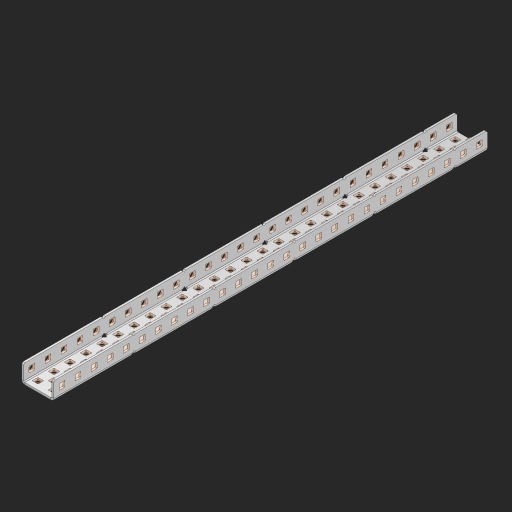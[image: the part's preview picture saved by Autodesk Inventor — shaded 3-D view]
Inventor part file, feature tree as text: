
AUTODESK INVENTOR PART (.ipt)
format: ipt  version: 2023 (Build 270158000, 158)  size: 1,725,440 bytes
history: native  units: in
note: dims shown in document units (in); Inventor stores cm internally (conversion verified against a paired STEP export)
features: other x142, extrude x133, sheet_metal_op x11, sketch x10, pattern_linear x2, mirror x1, chamfer x1
ambient origin geometry x8: Origin, YZ Plane, XZ Plane, XY Plane, X Axis, Y Axis, Z Axis, Center Point
bodies: Solid1 (feature_tree), Body (feature_tree)
feature tree (300):
  sheet_metal_op  "Flanges"
  other  "Flange Pattern Plane"
  other  "Flange Pattern Sketch"
  sheet_metal_op  "Flange Pattern"
  sheet_metal_op  "Body Pattern"
  pattern_linear  "Center Pattern"  Spacing1=0.0625in  [1 undecoded]
  other  "Arc Length"
  mirror  "Notch Mirror"
  pattern_linear  "Notch Pattern"  Spacing1=0.182in  [1 undecoded]
  chamfer  "End Chamfer"
  extrude  "Half Cut"  Depth=0.02in
  sketch  "Sketch1"  dims[d0=1.0in]
  other  "Plate1"
  sketch  "Sketch2"  dims[d1=13.5in]
  other  "Plate2"
  sheet_metal_op  "Bend1"
  sheet_metal_op  "Corner1"
  sketch  "Sketch3"  dims[d2=0.0625in]
  sketch  "Sketch7"  dims[d3=0.0625in]
  other  "Srf1"
  other  "Srf2"
  sketch  "Sketch8"  dims[d4=0.0312in]
  sketch  "Sketch9"  dims[d5=0.125in]
  other  "Srf91"
  sheet_metal_op  "Body Pattern Sketch"
  other  "Srf92"
  sketch  "Sketch13"  dims[d6=0.0625in]
  sketch  "Sketch14"  dims[d7=0.5in d8=90.0deg d9=0.0312in]
  sketch  "Sketch15"  dims[d10=0.25in]
  sketch  "Sketch16"  dims[d11=0.0625in d12=0.0625in d16=0.182in d17=0.02in d18=0.0625in d19=0.0in d20=0.25in d21=0.25in d38=10.6299in d40=0.5in d41=0.7874in d43=1.0in d46=0.172in d47=1.0in d48=0.0in d49=0.182in d50=0.02in d51=0.25in d52=0.25in d53=0.0625in d54=0.0in d55=0.172in d56=1.0in d57=0.0in d58=0.25in d60=10.6299in d62=0.5in d63=0.7874in d65=0.5in d85=0.1473in d86=0.1782in d88=0.04in d89=0.0625in d90=0.0in d91=0.04in d92=0.0491in d95=2.5in d96=0.04in d97=0.25in d98=45.0deg d99=0.25in d100=0.5in d101=0.0in d102=2.497in d106=0.182in d107=0.02in d108=0.5in d109=0.5in d110=0.0625in d111=0.0in d112=0.172in d113=0.5in d114=0.0in d117=0.5in d118=0.5in d119=0.5in]
  other  "Srf786"
  other  "Srf823"
  other  "Srf824"
  other  "Srf825"
  other  "Srf826"
  other  "Srf827"
  other  "Srf828"
  other  "Srf829"
  other  "Srf856"
  other  "Srf857"
  other  "Srf858"
  other  "Srf859"
  other  "Srf860"
  other  "Srf861"
  other  "Srf862"
  other  "Srf889"
  other  "Srf890"
  other  "Srf891"
  other  "Srf892"
  other  "Srf893"
  other  "Srf894"
  other  "Srf895"
  other  "Srf896"
  other  "Srf922"
  other  "Srf923"
  other  "Srf924"
  other  "Srf925"
  other  "Srf926"
  other  "Srf959"
  other  "Srf960"
  other  "Srf961"
  other  "Srf962"
  other  "Srf963"
  other  "Srf996"
  other  "Srf997"
  other  "Srf998"
  other  "Srf999"
  other  "Srf1000"
  other  "Srf1143"
  other  "Srf1144"
  other  "Srf1145"
  other  "Srf1146"
  other  "Srf1147"
  other  "Srf1148"
  other  "Srf1149"
  other  "Srf1150"
  other  "Srf1151"
  other  "Srf1152"
  other  "Srf1153"
  other  "Srf1154"
  other  "Srf1155"
  other  "Srf1156"
  other  "Srf1157"
  other  "Srf1158"
  other  "Srf1159"
  other  "Srf1160"
  other  "Srf1161"
  other  "Srf1162"
  other  "Srf1163"
  other  "Srf1164"
  other  "Srf1165"
  other  "Srf1166"
  other  "Srf1167"
  other  "Srf1168"
  other  "Srf1169"
  other  "Srf1170"
  other  "Srf1171"
  other  "Srf1172"
  other  "Srf1173"
  other  "Srf1174"
  other  "Srf1175"
  other  "Srf1176"
  other  "Srf1177"
  other  "Srf1178"
  other  "Srf1179"
  other  "Srf1180"
  other  "Srf1181"
  other  "Srf1182"
  other  "Srf1199"
  other  "Srf1200"
  other  "Srf1201"
  other  "Srf1202"
  other  "Srf1203"
  other  "Srf1204"
  other  "Srf1205"
  other  "Srf1206"
  other  "Srf1207"
  other  "Srf1208"
  other  "Srf1209"
  other  "Srf1210"
  other  "Srf1211"
  other  "Srf1212"
  other  "Srf1213"
  other  "Srf1214"
  other  "Srf1215"
  other  "Srf1216"
  other  "Srf1217"
  other  "Srf1218"
  other  "Srf1219"
  other  "Srf1220"
  other  "Srf1221"
  other  "Srf1222"
  other  "Srf1223"
  other  "Srf1224"
  other  "Srf1225"
  other  "Srf1226"
  other  "Srf1227"
  other  "Srf1228"
  other  "Srf1229"
  other  "Srf1230"
  other  "Srf1231"
  other  "Srf1232"
  other  "Srf1233"
  other  "Srf1234"
  other  "Srf1235"
  other  "Srf1236"
  other  "Srf1237"
  other  "Srf1238"
  other  "Srf1255"
  other  "Srf1256"
  other  "Srf1257"
  other  "Srf1258"
  other  "Srf1259"
  other  "Srf1260"
  other  "Srf1261"
  other  "Srf1262"
  other  "Srf1263"
  other  "Srf1264"
  other  "Srf1265"
  other  "Srf1266"
  other  "Srf1267"
  sheet_metal_op  "Flange Stamp"
  sheet_metal_op  "Flange Circle"
  sheet_metal_op  "Body Stamp"
  sheet_metal_op  "Body Circle"
  other  "Center Stamp"
  other  "Center Circle"
  sheet_metal_op  "Notch"
  extrude  "ExtrusionSrf2"  Depth=0.0625in
  extrude  "ExtrusionSrf92"  TaperAngle=0.0deg  [1 undecoded]
  extrude  "ExtrusionSrf823"  Depth=0.5in
  extrude  "ExtrusionSrf824"  Depth=0.5in
  extrude  "ExtrusionSrf825"  Depth=0.5in
  extrude  "ExtrusionSrf826"  Depth=0.5in
  extrude  "ExtrusionSrf827"  Depth=1.0in TaperAngle=0.0deg
  extrude  "ExtrusionSrf828"  Depth=0.5in
  extrude  "ExtrusionSrf829"  Depth=0.02in
  extrude  "ExtrusionSrf856"  Depth=0.5in
  extrude  "ExtrusionSrf857"  Depth=0.5in
  extrude  "ExtrusionSrf858"  Depth=0.0625in
  extrude  "ExtrusionSrf859"  TaperAngle=0.0deg  [1 undecoded]
  extrude  "ExtrusionSrf860"  Depth=0.5in
  extrude  "ExtrusionSrf861"  Depth=1.0in TaperAngle=0.0deg
  extrude  "ExtrusionSrf862"  Depth=0.5in
  extrude  "ExtrusionSrf889"  Depth=0.5in
  extrude  "ExtrusionSrf890"  Depth=0.5in
  extrude  "ExtrusionSrf891"  Depth=0.5in
  extrude  "ExtrusionSrf892"  Depth=0.5in
  extrude  "ExtrusionSrf893"  Depth=0.5in
  extrude  "ExtrusionSrf894"  Depth=0.0625in
  extrude  "ExtrusionSrf895"  TaperAngle=0.0deg  [1 undecoded]
  extrude  "ExtrusionSrf896"  Depth=0.5in
  extrude  "ExtrusionSrf922"  Depth=0.5in
  extrude  "ExtrusionSrf923"  Depth=2.5in
  extrude  "ExtrusionSrf924"  Depth=0.5in TaperAngle=45.0deg
  extrude  "ExtrusionSrf925"  Depth=0.5in
  extrude  "ExtrusionSrf926"  Depth=0.5in TaperAngle=0.0deg
  extrude  "ExtrusionSrf959"  Depth=0.5in
  extrude  "ExtrusionSrf960"  Depth=0.5in
  extrude  "ExtrusionSrf961"  Depth=0.02in
  extrude  "ExtrusionSrf962"  Depth=0.5in
  extrude  "ExtrusionSrf963"  Depth=0.5in
  extrude  "ExtrusionSrf996"  Depth=0.0625in
  extrude  "ExtrusionSrf997"  TaperAngle=0.0deg  [1 undecoded]
  extrude  "ExtrusionSrf998"  Depth=0.5in
  extrude  "ExtrusionSrf999"  Depth=0.5in TaperAngle=0.0deg
  extrude  "ExtrusionSrf1000"  Depth=0.5in
  extrude  "ExtrusionSrf1143"  Depth=0.5in
  extrude  "ExtrusionSrf1144"  Depth=0.5in
  extrude  "ExtrusionSrf1145"  [1 undecoded]
  extrude  "ExtrusionSrf1146"  [1 undecoded]
  extrude  "ExtrusionSrf1147"  [1 undecoded]
  extrude  "ExtrusionSrf1148"  [1 undecoded]
  extrude  "ExtrusionSrf1149"  [1 undecoded]
  extrude  "ExtrusionSrf1150"  [1 undecoded]
  extrude  "ExtrusionSrf1151"  [1 undecoded]
  extrude  "ExtrusionSrf1152"  [1 undecoded]
  extrude  "ExtrusionSrf1153"  [1 undecoded]
  extrude  "ExtrusionSrf1154"  [1 undecoded]
  extrude  "ExtrusionSrf1155"  [1 undecoded]
  extrude  "ExtrusionSrf1156"  [1 undecoded]
  extrude  "ExtrusionSrf1157"  [1 undecoded]
  extrude  "ExtrusionSrf1158"  [1 undecoded]
  extrude  "ExtrusionSrf1159"  [1 undecoded]
  extrude  "ExtrusionSrf1160"  [1 undecoded]
  extrude  "ExtrusionSrf1161"  [1 undecoded]
  extrude  "ExtrusionSrf1162"  [1 undecoded]
  extrude  "ExtrusionSrf1163"  [1 undecoded]
  extrude  "ExtrusionSrf1164"  [1 undecoded]
  extrude  "ExtrusionSrf1165"  [1 undecoded]
  extrude  "ExtrusionSrf1166"  [1 undecoded]
  extrude  "ExtrusionSrf1167"  [1 undecoded]
  extrude  "ExtrusionSrf1168"  [1 undecoded]
  extrude  "ExtrusionSrf1169"  [1 undecoded]
  extrude  "ExtrusionSrf1170"  [1 undecoded]
  extrude  "ExtrusionSrf1171"  [1 undecoded]
  extrude  "ExtrusionSrf1172"  [1 undecoded]
  extrude  "ExtrusionSrf1173"  [1 undecoded]
  extrude  "ExtrusionSrf1174"  [1 undecoded]
  extrude  "ExtrusionSrf1175"  [1 undecoded]
  extrude  "ExtrusionSrf1176"  [1 undecoded]
  extrude  "ExtrusionSrf1177"  [1 undecoded]
  extrude  "ExtrusionSrf1178"  [1 undecoded]
  extrude  "ExtrusionSrf1179"  [1 undecoded]
  extrude  "ExtrusionSrf1180"  [1 undecoded]
  extrude  "ExtrusionSrf1181"  [1 undecoded]
  extrude  "ExtrusionSrf1182"  [1 undecoded]
  extrude  "ExtrusionSrf1199"  [1 undecoded]
  extrude  "ExtrusionSrf1200"  [1 undecoded]
  extrude  "ExtrusionSrf1201"  [1 undecoded]
  extrude  "ExtrusionSrf1202"  [1 undecoded]
  extrude  "ExtrusionSrf1203"  [1 undecoded]
  extrude  "ExtrusionSrf1204"  [1 undecoded]
  extrude  "ExtrusionSrf1205"  [1 undecoded]
  extrude  "ExtrusionSrf1206"  [1 undecoded]
  extrude  "ExtrusionSrf1207"  [1 undecoded]
  extrude  "ExtrusionSrf1208"  [1 undecoded]
  extrude  "ExtrusionSrf1209"  [1 undecoded]
  extrude  "ExtrusionSrf1210"  [1 undecoded]
  extrude  "ExtrusionSrf1211"  [1 undecoded]
  extrude  "ExtrusionSrf1212"  [1 undecoded]
  extrude  "ExtrusionSrf1213"  [1 undecoded]
  extrude  "ExtrusionSrf1214"  [1 undecoded]
  extrude  "ExtrusionSrf1215"  [1 undecoded]
  extrude  "ExtrusionSrf1216"  [1 undecoded]
  extrude  "ExtrusionSrf1217"  [1 undecoded]
  extrude  "ExtrusionSrf1218"  [1 undecoded]
  extrude  "ExtrusionSrf1219"  [1 undecoded]
  extrude  "ExtrusionSrf1220"  [1 undecoded]
  extrude  "ExtrusionSrf1221"  [1 undecoded]
  extrude  "ExtrusionSrf1222"  [1 undecoded]
  extrude  "ExtrusionSrf1223"  [1 undecoded]
  extrude  "ExtrusionSrf1224"  [1 undecoded]
  extrude  "ExtrusionSrf1225"  [1 undecoded]
  extrude  "ExtrusionSrf1226"  [1 undecoded]
  extrude  "ExtrusionSrf1227"  [1 undecoded]
  extrude  "ExtrusionSrf1228"  [1 undecoded]
  extrude  "ExtrusionSrf1229"  [1 undecoded]
  extrude  "ExtrusionSrf1230"  [1 undecoded]
  extrude  "ExtrusionSrf1231"  [1 undecoded]
  extrude  "ExtrusionSrf1232"  [1 undecoded]
  extrude  "ExtrusionSrf1233"  [1 undecoded]
  extrude  "ExtrusionSrf1234"  [1 undecoded]
  extrude  "ExtrusionSrf1235"  [1 undecoded]
  extrude  "ExtrusionSrf1236"  [1 undecoded]
  extrude  "ExtrusionSrf1237"  [1 undecoded]
  extrude  "ExtrusionSrf1238"  [1 undecoded]
  extrude  "ExtrusionSrf1255"  [1 undecoded]
  extrude  "ExtrusionSrf1256"  [1 undecoded]
  extrude  "ExtrusionSrf1257"  [1 undecoded]
  extrude  "ExtrusionSrf1258"  [1 undecoded]
  extrude  "ExtrusionSrf1259"  [1 undecoded]
  extrude  "ExtrusionSrf1260"  [1 undecoded]
  extrude  "ExtrusionSrf1261"  [1 undecoded]
  extrude  "ExtrusionSrf1262"  [1 undecoded]
  extrude  "ExtrusionSrf1263"  [1 undecoded]
  extrude  "ExtrusionSrf1264"  [1 undecoded]
  extrude  "ExtrusionSrf1265"  [1 undecoded]
  extrude  "ExtrusionSrf1266"  [1 undecoded]
  extrude  "ExtrusionSrf1267"  [1 undecoded]
note: 97 required parameter values undecoded (feature->parameter linkage not recoverable at this tier; creation-order binding heuristic only, values carry confidence <= 0.55)
